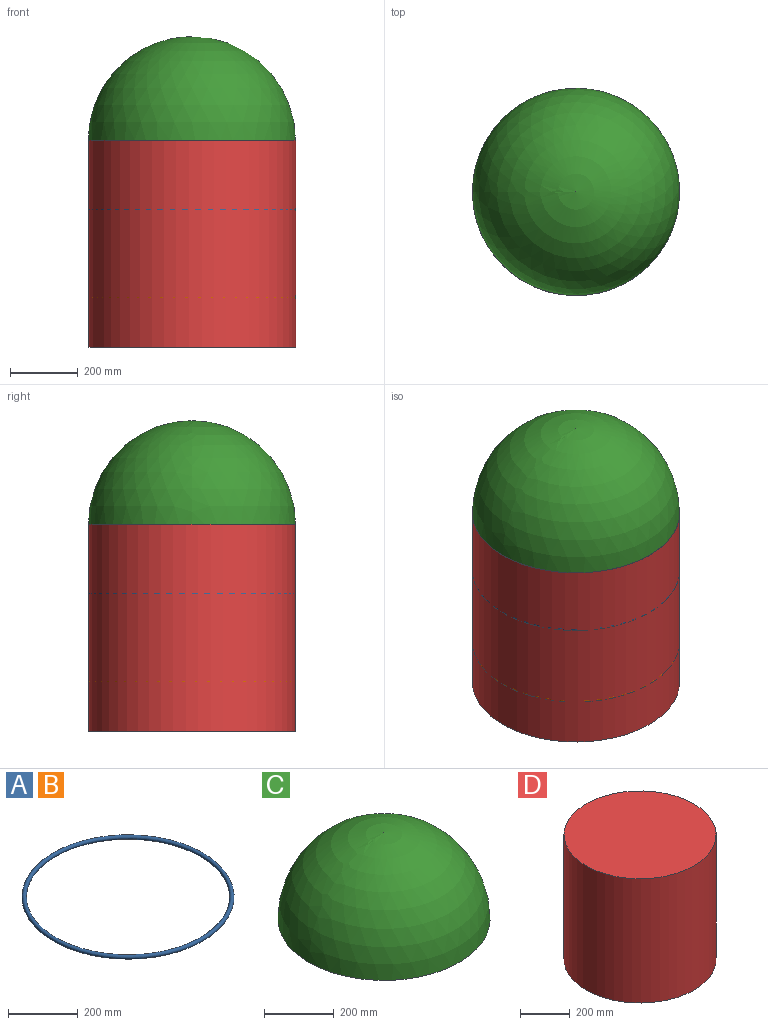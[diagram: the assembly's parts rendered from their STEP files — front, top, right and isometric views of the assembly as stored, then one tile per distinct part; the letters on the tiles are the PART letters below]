
ASSEMBLY  parts=4 mates=3
PART A: 1 faces, bbox 659.8x659.8x12.7 mm
  f0: torus R=298.45mm, axis (0,0,1), area 74817.8mm2
PART B: same geometry as A
PART C: 2 faces, bbox 609.6x609.6x304.8 mm
  f0: plane 609.6x609.6mm, normal (0,0,-1), area 291863.5mm2, adj f1
  f1: sphere r=304.8mm, area 583727mm2, adj f0
PART D: 3 faces, bbox 609.6x609.6x609.6 mm
  f0: cylinder r=304.8mm len=609.6mm, axis (0,0,-1), area 1167454mm2, adj f1,f2
  f1: plane 609.6x609.6mm, normal (0,0,1), area 291863.5mm2, adj f0
  f2: plane 609.6x609.6mm, normal (0,0,-1), area 291863.5mm2, adj f0
PLACE A rot(axis=(0,0,-1),0.8deg) t=(304.68,437.43,-79.93)mm
PLACE B rot(axis=(0,0,-1),0.7deg) t=(304.68,437.43,-337.55)mm
PLACE C t=(304.68,437.43,124.2)mm fixed
PLACE D t=(304.68,437.43,-485.4)mm
MATE fastened D.f0 <-> C.f0  axis (0,0,1) through (304.68,437.43,124.2)mm
MATE cylindrical B.f0 <-> D.f0  axis (0,0,1) through (304.68,437.43,-337.55)mm
MATE cylindrical A.f0 <-> D.f0  axis (0,0,1) through (304.68,437.43,-79.93)mm
